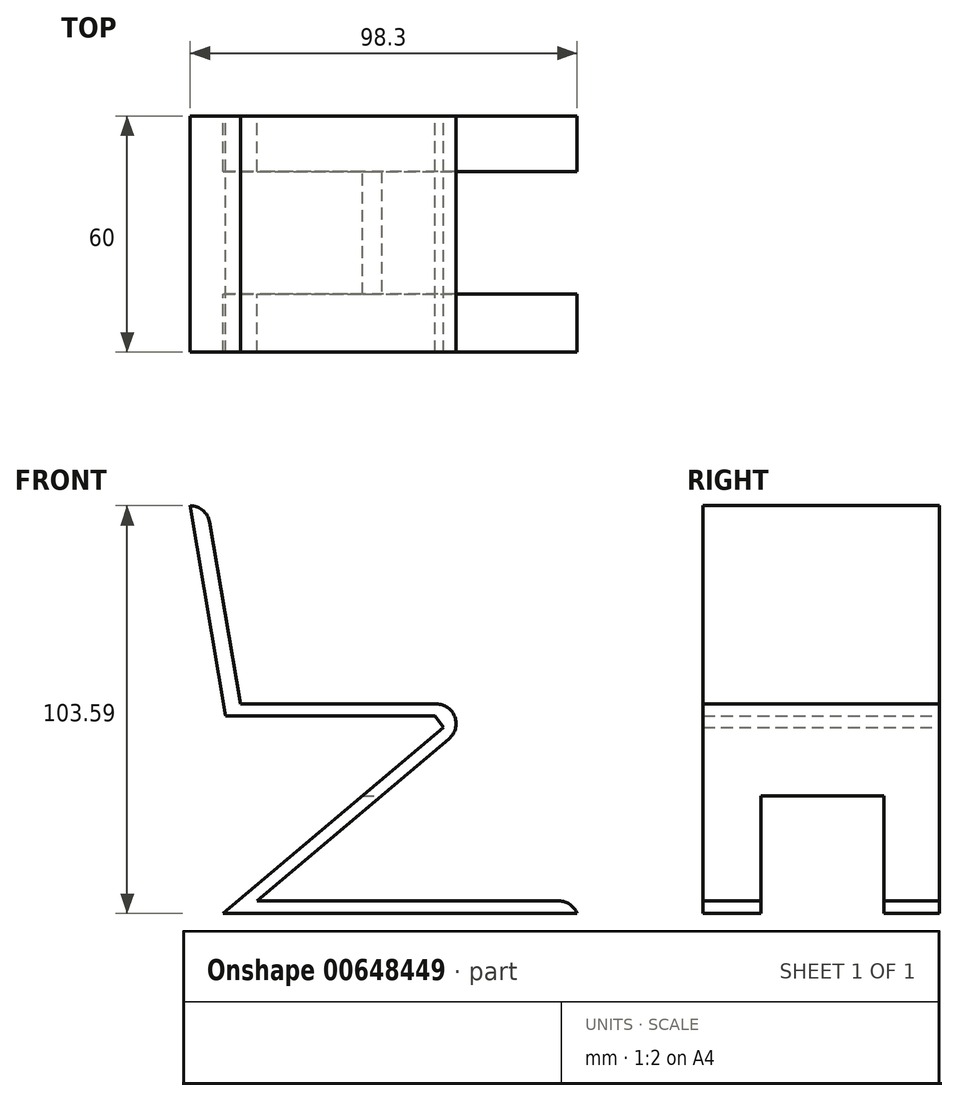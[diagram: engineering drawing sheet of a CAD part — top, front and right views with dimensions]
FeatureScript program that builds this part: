
annotation { "Feature Type Name" : "Feature", "Feature Type Description" : "" }
export const myFeature = defineFeature(function(context is Context, id is Id, definition is map)
    precondition{}
    {
        {
            var Q0;
            Q0=qCreatedBy(makeId("Front.planeOp"),FACE);
            var sketch = newSketch(context, id + "F0", { "sketchPlane" : qUnion([Q0])});
            skLineSegment(sketch, "E0", {"start": v(-47.16, 53.4) * mm, "end": v(-38.12, 0) * mm});
            skLineSegment(sketch, "E1", {"start": v(-38.12, 0) * mm, "end": v(15.01, 0) * mm});
            skLineSegment(sketch, "E2", {"start": v(15.01, 0) * mm, "end": v(17.14, -2.92) * mm});
            skLineSegment(sketch, "E3", {"start": v(17.14, -2.92) * mm, "end": v(-27.5, -40.65) * mm});
            skLineSegment(sketch, "E4", {"start": v(-27.5, -40.65) * mm, "end": v(-38.8, -50.2) * mm});
            skLineSegment(sketch, "E5", {"start": v(-38.8, -50.2) * mm, "end": v(51.14, -50.2) * mm});
            skLineSegment(sketch, "E6", {"start": v(51.14, -50.2) * mm, "end": v(51.14, -47.02) * mm});
            skLineSegment(sketch, "E7", {"start": v(51.14, -47.02) * mm, "end": v(-30.15, -47.02) * mm});
            skLineSegment(sketch, "E8", {"start": v(-30.15, -47.02) * mm, "end": v(19.5, -5.06) * mm});
            skLineSegment(sketch, "E9", {"start": v(19.5, -5.06) * mm, "end": v(29.04, 3) * mm});
            skLineSegment(sketch, "E10", {"start": v(29.04, 3) * mm, "end": v(-34.4, 3) * mm});
            skLineSegment(sketch, "E11", {"start": v(-34.4, 3) * mm, "end": v(-43.13, 54.6) * mm});
            skLineSegment(sketch, "E12", {"start": v(-43.13, 54.6) * mm, "end": v(-47.16, 53.4) * mm});
            skSolve(sketch);
        }
        {
            var Q0;
            Q0 = qSketchRegion(id + "F0", true);
            extrude(context, id + "F1", {"entities" : qUnion([Q0]), "depth" : 60 * mm, "offsetDistance" : 25 * mm});
        }
        {
            var Q0;
            Q0=makeQuery(id+"F1.opExtrude","SWEPT_EDGE",EDGE,{"disambiguationData":[OSD([sQuery(id+"F0.wireOp",EDGE,"E9"),sQuery(id+"F0.wireOp",EDGE,"E10")])]});
            var Q1;
            Q1=makeQuery(id+"F1.opExtrude","SWEPT_EDGE",EDGE,{"disambiguationData":[OSD([sQuery(id+"F0.wireOp",EDGE,"E11"),sQuery(id+"F0.wireOp",EDGE,"E12")])]});
            var Q2;
            Q2=makeQuery(id+"F1.opExtrude","SWEPT_EDGE",EDGE,{"disambiguationData":[OSD([sQuery(id+"F0.wireOp",EDGE,"E6"),sQuery(id+"F0.wireOp",EDGE,"E7")])]});
            fillet(context, id + "F2", {"entities" : qUnion([Q0, Q1, Q2]), "radius" : 5 * mm, "tangentPropagation" : true, "allowEdgeOverflow" : false});
        }
        {
            var Q0;
            Q0=qCreatedBy(makeId("Right.planeOp"),FACE);
            var sketch = newSketch(context, id + "F3", { "sketchPlane" : qUnion([Q0])});
            skLineSegment(sketch, "E13.bottom", {"start": v(-45.25, -20.28) * mm, "end": v(-14.04, -20.28) * mm});
            skLineSegment(sketch, "E13.top", {"start": v(-45.25, -73.72) * mm, "end": v(-14.04, -73.72) * mm});
            skLineSegment(sketch, "E13.left", {"start": v(-45.25, -20.28) * mm, "end": v(-45.25, -73.72) * mm});
            skLineSegment(sketch, "E13.right", {"start": v(-14.04, -20.28) * mm, "end": v(-14.04, -73.72) * mm});
            skSolve(sketch);
        }
        {
            var Q0;
            Q0 = qSketchRegion(id + "F3", true);
            extrude(context, id + "F4", {"entities" : qUnion([Q0]), "operationType" : NewBodyOperationType.REMOVE, "endBound" : BoundingType.THROUGH_ALL, "oppositeDirection" : true, "depth" : 25 * mm, "offsetDistance" : 25 * mm, "hasSecondDirection" : true, "secondDirectionOppositeDirection" : false, "secondDirectionDepth" : 100 * mm});
        }
    });
